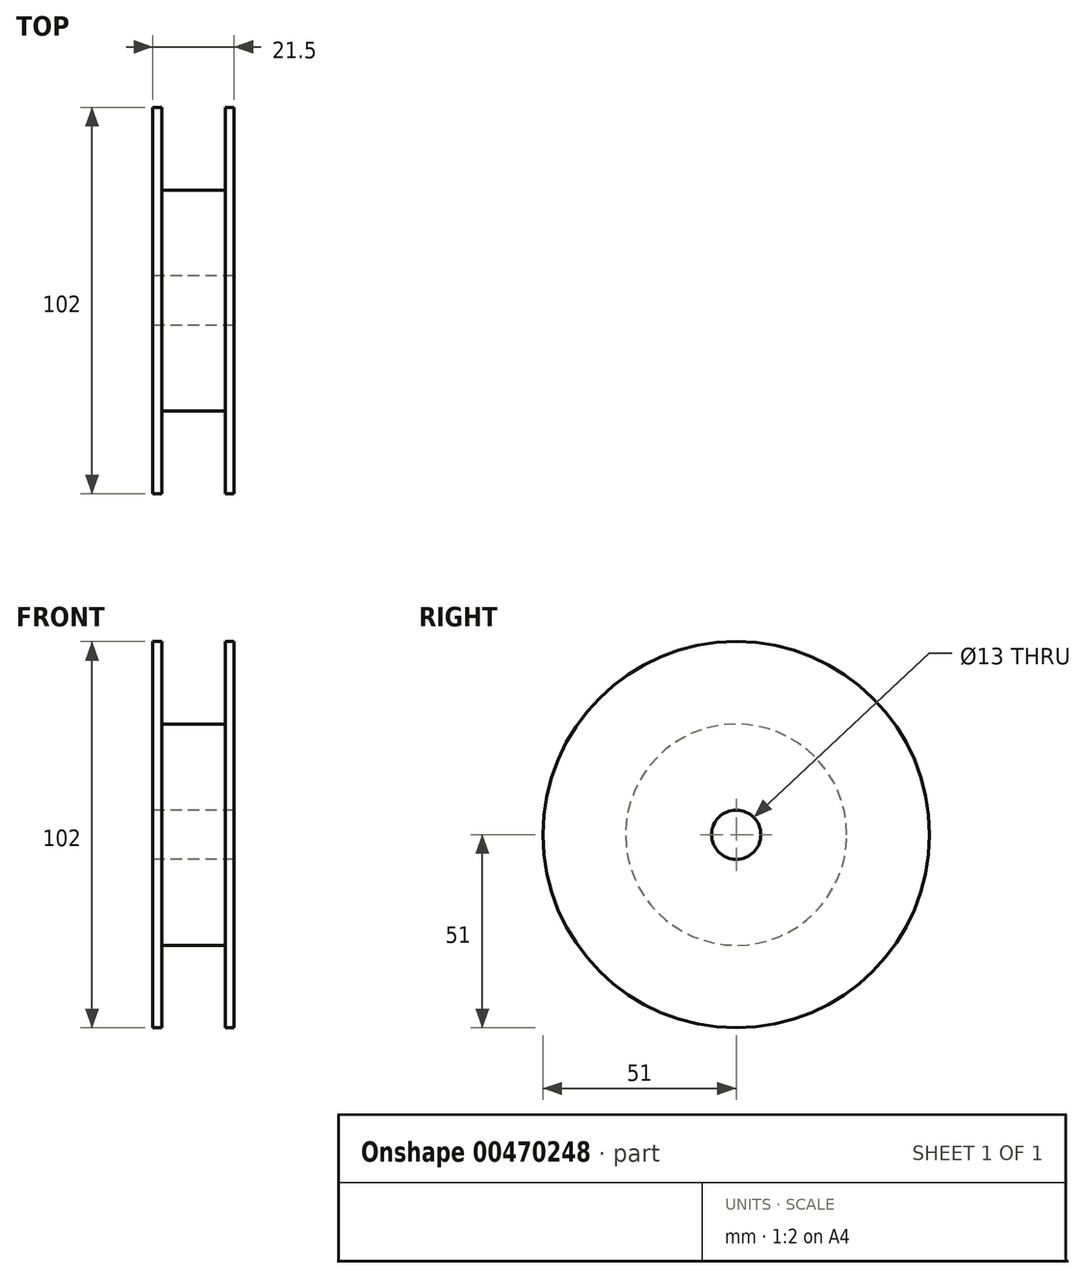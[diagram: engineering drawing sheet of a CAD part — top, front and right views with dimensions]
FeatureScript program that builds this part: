
annotation { "Feature Type Name" : "Feature", "Feature Type Description" : "" }
export const myFeature = defineFeature(function(context is Context, id is Id, definition is map)
    precondition{}
    {
        {
            var Q0;
            Q0=qCreatedBy(makeId("Front.planeOp"),FACE);
            var sketch = newSketch(context, id + "F0", { "sketchPlane" : qUnion([Q0])});
            skLineSegment(sketch, "E0", {"start": v(-10.75, 6.5) * mm, "end": v(-10.75, 51) * mm});
            skLineSegment(sketch, "E1", {"start": v(-10.75, 51) * mm, "end": v(-8.37, 51) * mm});
            skLineSegment(sketch, "E2", {"start": v(-8.37, 51) * mm, "end": v(-8.37, 29.2) * mm});
            skLineSegment(sketch, "E3", {"start": v(-8.37, 29.2) * mm, "end": v(0, 29.2) * mm});
            skLineSegment(sketch, "E4", {"start": v(-10.75, 6.5) * mm, "end": v(0, 6.5) * mm});
            skLineSegment(sketch, "E5.MirrorCS", {"start": v(10.75, 51) * mm, "end": v(8.37, 51) * mm});
            skLineSegment(sketch, "E6.MirrorCS", {"start": v(10.75, 6.5) * mm, "end": v(10.75, 51) * mm});
            skLineSegment(sketch, "E7.MirrorCS", {"start": v(8.37, 51) * mm, "end": v(8.37, 29.2) * mm});
            skLineSegment(sketch, "E8.MirrorCS", {"start": v(8.37, 29.2) * mm, "end": v(0, 29.2) * mm});
            skLineSegment(sketch, "E9.MirrorCS", {"start": v(10.75, 6.5) * mm, "end": v(0, 6.5) * mm});
            skLineSegment(sketch, "E10", {"start": v(-27.39, 0) * mm, "end": v(29.48, 0) * mm, "construction": true});
            skSolve(sketch);
        }
        {
            var Q0;
            Q0 = qSketchRegion(id + "F0", true);
            var Q1;
            Q1=sQuery(id+"F0.wireOp",EDGE,"E10");
            revolve(context, id + "F1", {"entities" : qUnion([Q0]), "axis" : qUnion([Q1]), "revolveType" : RevolveType.FULL});
        }
        {
            var Q0;
            Q0=qCreatedBy(makeId("Front.planeOp"),FACE);
            var sketch = newSketch(context, id + "F2", { "sketchPlane" : qUnion([Q0])});
            skLineSegment(sketch, "E11.bottom", {"start": v(8.32, 29.51) * mm, "end": v(-8.32, 29.51) * mm});
            skLineSegment(sketch, "E11.top", {"start": v(8.32, 48.51) * mm, "end": v(-8.32, 48.51) * mm});
            skLineSegment(sketch, "E11.left", {"start": v(8.32, 29.51) * mm, "end": v(8.32, 48.51) * mm});
            skLineSegment(sketch, "E11.right", {"start": v(-8.33, 29.51) * mm, "end": v(-8.33, 48.51) * mm});
            skPoint(sketch, "E11.middle", {"position": v(0, 39.01) * mm});
            skSolve(sketch);
        }
        {
            var Q0;
            Q0=makeQuery(id+"F2.imprint","IMPRINT",FACE,{"disambiguationData":[TD([[makeQuery(id+"F2.imprint","IMPRINT",EDGE,{"derivedFrom":sQuery(id+"F2.wireOp",EDGE,"E11.bottom")}),-1.0]])]});
            var Q1;
            Q1 = qConstructionFilter(qBodyType(qCreatedBy(id + "F2" ,EDGE), BodyType.WIRE), ConstructionObject.NO);
            var Q2;
            Q2=sQuery(id+"F0.wireOp",EDGE,"E10");
            revolve(context, id + "F3", {"bodyType" : ToolBodyType.SURFACE, "entities" : qUnion([Q0]), "surfaceEntities" : qUnion([Q1]), "axis" : qUnion([Q2]), "revolveType" : RevolveType.FULL});
        }
    });
